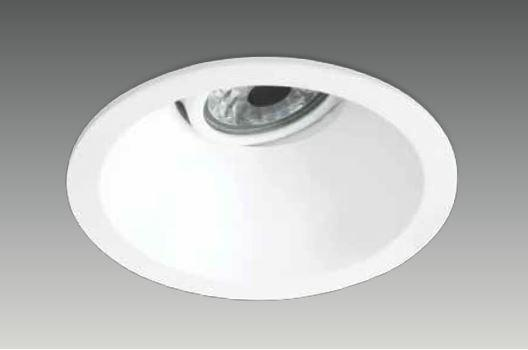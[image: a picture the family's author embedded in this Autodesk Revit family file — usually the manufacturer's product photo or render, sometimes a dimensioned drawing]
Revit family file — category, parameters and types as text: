
# Revit family: DG 1011 SAY
name_source: partatom
category: Lighting Fixtures
revit_build: Autodesk Revit 2017 (Build: 20160225_1515(x64)
units: mm (PartAtom-declared; Revit-internal decimal feet)

## family parameters
Always vertical = Yes
Cut with Voids When Loaded = No
Host = Ceiling
Light Source = Yes
OmniClass Number = 23.80.70.11
OmniClass Title = Luminaries for Internal Lighting
Part Type = Normal
Room Calculation Point = No
Round Connector Dimension = Use Diameter
Shared = No

## types (18) — shared parameters
Color Filter = 16777215
Dimming Lamp Color Temperature Shift = <None>
Emit Shape Visible in Rendering = Yes
Emit from Circle Diameter = 80 mm  [stored 0.262467 ft]
Light Source Symbol Length = 3048 mm  [stored 10 ft]
Manufacturer = ARLIGHT
Spot Field Angle = 90.00°
Tilt Angle = 90.00°
Type Image = DG 1011 SAY.JPG

## per-type parameters (varying)
| type | Apparent Load | Spot Beam Angle | Wattage Comments |
| DGSAY.110.8.30.25 | 8 VA | 25.00° | 8W |
| DGSAY.110.8.40.25 | 8 VA | 25.00° | 8W |
| DGSAY.110.8.30.35 | 8 VA | 35.00° | 8W |
| DGSAY.110.8.40.35 | 8 VA | 35.00° | 8W |
| DGSAY.110.8.30.60 | 8 VA | 60.00° | 8W |
| DGSAY.110.8.40.60 | 8 VA | 60.00° | 8W |
| DGSAY.110.6.30.25 | 6 VA | 25.00° | 6W |
| DGSAY.110.6.40.25 | 6 VA | 25.00° | 6W |
| DGSAY.110.6.30.35 | 6 VA | 35.00° | 6W |
| DGSAY.110.6.40.35 | 6 VA | 35.00° | 6W |
| DGSAY.110.6.30.60 | 6 VA | 60.00° | 6W |
| DGSAY.110.6.40.60 | 6 VA | 60.00° | 6W |
| DGSAY.110.11.30.25 | 11 VA | 25.00° | 11W |
| DGSAY.110.11.40.25 | 11 VA | 25.00° | 11W |
| DGSAY.110.11.30.35 | 11 VA | 35.00° | 11W |
| DGSAY.110.11.40.35 | 11 VA | 35.00° | 11W |
| DGSAY.110.11.30.60 | 11 VA | 60.00° | 11W |
| DGSAY.110.11.40.60 | 11 VA | 60.00° | 11W |

note: [stored X ft] marks values corroborated as IEEE doubles in the binary element streams (Revit-internal decimal feet)

## geometry (parser evidence)
native form markers: Sweep x3
no freeform markers — native parametric forms only
